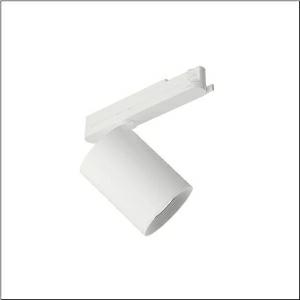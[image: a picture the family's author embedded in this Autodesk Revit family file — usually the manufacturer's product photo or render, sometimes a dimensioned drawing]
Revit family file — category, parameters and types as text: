
# Revit family: spot_21_51se13dba5b
name_source: partatom
category: Lighting Fixtures
units: mm (PartAtom-declared; Revit-internal decimal feet)

## family parameters
Cut with Voids When Loaded = No
Host = Face
Light Source = No
Part Type = Normal
Room Calculation Point = No
Round Connector Dimension = Use Diameter
Shared = No

## types (1)
- --- (1 x LED, 5190 lm, 42.4 W, 2700K)
    Apparent Load = 42 VA
    CIE Flux Codes = 95 98 99 100 100
    Color Rendering = 90
    Color Temperature = 2700K
    Default Elevation = 1800 mm
    Description = Spot 21, directional spotlight, light control with lens, of PMMA, LED rated luminous flux: 4.960lm, light colour: 927, control gear: ECG Multilumen, with 3-phase adapter, mains connection: 220..240V, AC, 50/60Hz, of aluminium, traffic white (RAL 9016), length: 253mm, diameter: 105mm, protection rating (complete): IP20, insulation class (complete): insulation class I (protective earthing), certification: CE, impact resistance: IK02, permissible ambient temperature for indoor applications: -20..+40°C, packaging unit: 1 piece
    Height = 175 mm
    Lamp = 1 x LED
    Lamp Light Flux = 5190 lm
    Lamp Power = 42.4 W
    Lamp count = 1
    Length = 105 mm
    Luminous efficacy = 122 lm/W
    Manufacturer = Siteco
    ModVariant = No
    Model = 51SE13DBA5B
    Mounting Place = Ceiling
    Mounting Type = Pendant
    Number of Poles = 1
    OnlyDefault = Yes
    Power Factor = 1
    Product Name = Spot 21
    Product group = directional spotlight
    ProductGroupID = 905
    Protection Class = Protection class I
    Protection Degree = IP 20
    RLX_Detail_Level = 1
    RLX_Emergency_Light_Flux = 0 lm
    RLX_Emergency_Type = 0
    RLX_Emergency_Type_DB = No
    RlxData = <blob elided: 17581 chars, md5=613c75d3>
    Socket = socket
    Standby Power = 0 W
    System Light Flux = 5190 lm
    System Power = 42 W
    Type Comments = factory setting: luminous flux: 100 % | (ON | ON | ON | ON) | 1050 mA
    Type Image = l_1003976.jpg
    URL = http://relux.com
    VarID = @adj_165217
    Voltage = 0 V
    Weight = 0.00 kg
    Width = 0 mm  [stored 0 ft]

note: [stored X ft] marks values corroborated as IEEE doubles in the binary element streams (Revit-internal decimal feet)

## geometry (parser evidence)
native form markers: Blend x4, Sweep x9
no freeform markers — native parametric forms only
